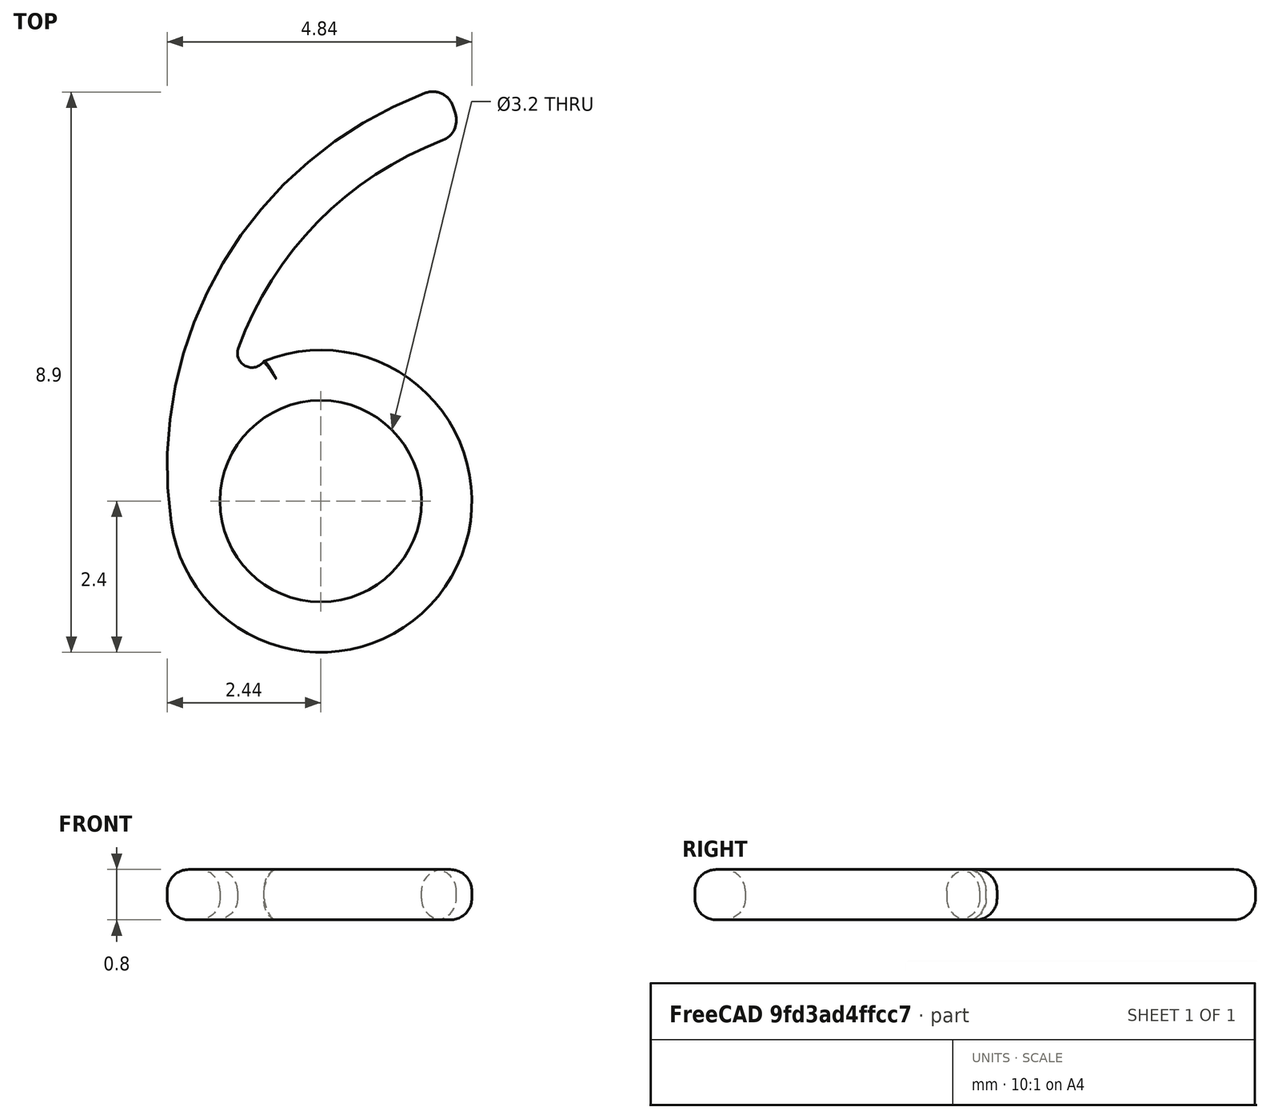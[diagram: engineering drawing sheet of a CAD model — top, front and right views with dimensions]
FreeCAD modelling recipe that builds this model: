
FCSTD DOCUMENT  (FreeCAD 0.16R6712 (Git))
Label: 6f
License: All rights reserved
LicenseURL: http://en.wikipedia.org/wiki/All_rights_reserved
objects: Sketcher::SketchObject×1, PartDesign::Pad×1, PartDesign::Fillet×1, Mesh::Feature×1
note: 4 computed .brp shape members not serialized (recipe doc carries the construction recipe); baked Part::Feature solids carry a one-line shape summary decoded from their .brp

FEATURE [Sketcher::SketchObject] Sketch
  sketch-geometry (6):
    g0: ArcOfCircle CenterX=3.9087 CenterY=2.94779 CenterZ=0 NormalX=0 NormalY=0 NormalZ=1 Radius=6.34689 StartAngle=1.87672 EndAngle=3.28083
    g1: ArcOfCircle CenterX=-1.09226 CenterY=4.75329 CenterZ=0 NormalX=0 NormalY=0 NormalZ=1 Radius=0.23 StartAngle=2.79515 EndAngle=5.68649
    g2: ArcOfCircle CenterX=0 CenterY=2.4 CenterZ=0 NormalX=0 NormalY=0 NormalZ=1 Radius=2.4 StartAngle=3.28083 EndAngle=8.23928
    g3: ArcOfCircle CenterX=3.9087 CenterY=2.94779 CenterZ=0 NormalX=0 NormalY=0 NormalZ=1 Radius=5.54689 StartAngle=1.87672 EndAngle=2.79513
    g4: LineSegment StartX=1.99719 StartY=9 StartZ=0 EndX=2.23813 EndY=8.23714 EndZ=0
    g5: Circle CenterX=0 CenterY=2.4 CenterZ=0 NormalX=0 NormalY=0 NormalZ=1 Radius=1.6
  constraints (16):
    c: Tangent(g0,g2) = -1.5708
    c: Radius(g2) = 2.4
    c: PointOnObject(g2,g-2)
    c: Coincident(g2,g1)
    c: Coincident(g1,g3)
    c: Tangent(g1,g3)
    c: Coincident(g4,g0)
    c: Coincident(g4,g3)
    c: Radius(g1) = 0.23
    c: PointOnObject(g-1,g2)
    c: Radius(g5) = 1.6
    c: Coincident(g2,g5)
    c: DistanceY(g-1,g0) = 9
    c: Coincident(g0,g3)
    c: Perpendicular(g3,g4)
    c: Distance(g3,g0) = 0.8
FEATURE [PartDesign::Pad] Pad
  Length = 0.8
  Length2 = 100
  Midplane = true
  Sketch = -> Sketch
  Type = 0
FEATURE [PartDesign::Fillet] Fillet
  Base = -> Pad [Edge4,Edge7,Edge10,Edge13,Edge15,Edge18,Edge1,Edge11,Edge14,Edge3,Edge6,Edge9,Edge12,Edge17]
  Radius = 0.34
FEATURE [Mesh::Feature] Mesh  label="Fillet (Meshed)"
